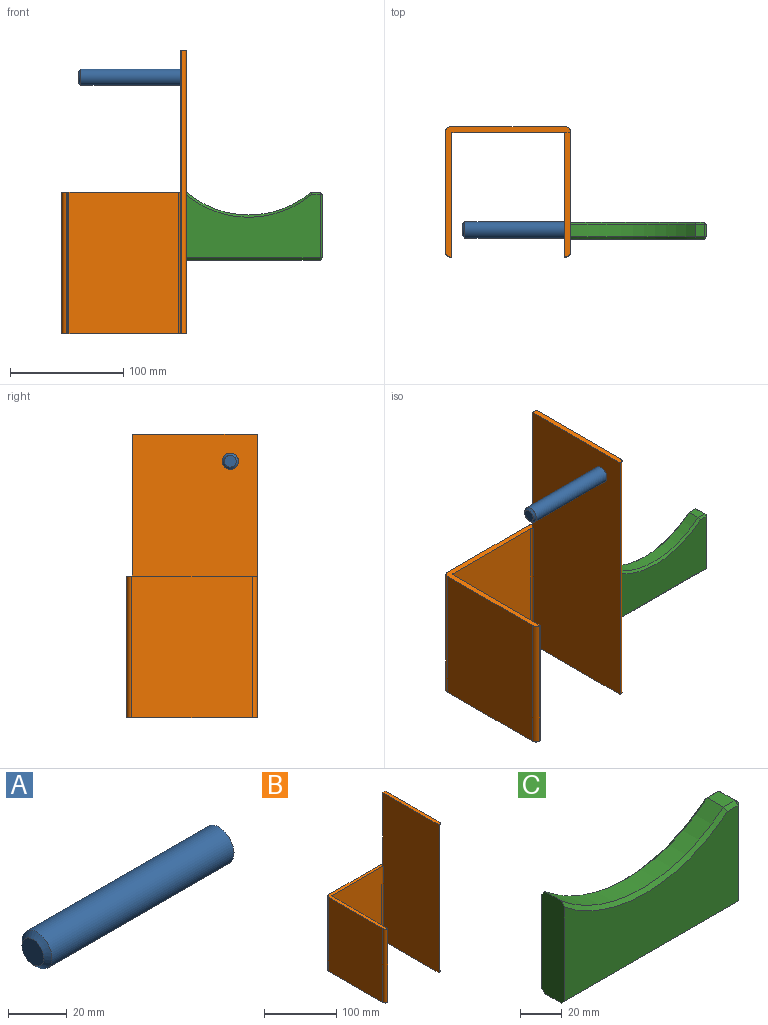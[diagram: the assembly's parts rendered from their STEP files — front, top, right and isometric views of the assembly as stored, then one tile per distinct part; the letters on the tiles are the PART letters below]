
ASSEMBLY  parts=3 mates=2
PART A: 4 faces, bbox 90x14.5x14.5 mm
  f0: cylinder r=7.25mm len=88mm, axis (-1,0,0), area 4008.7mm2, adj f1,f3
  f1: plane 14.5x14.5mm, normal (1,0,0), area 165.1mm2, adj f0
  f2: plane 10.5x10.5mm, normal (-1,0,0), area 86.6mm2, adj f3
  f3: cone r=7.25mm half-angle=45deg, axis (1,0,0), area 111.1mm2, adj f0,f2
PART B: 18 faces, bbox 110x115x250 mm
  f0: plane 250x106mm, normal (1,0,0), area 26437.5mm2, adj f1,f9,f10,f12,f13,f17
  f1: plane 110x5mm, normal (0,0,1), area 545.7mm2, adj f0,f3,f6,f12,f17
  f2: plane 125x0.5mm, normal (0,-1,0), area 62.5mm2, adj f4,f9,f10,f11
  f3: plane 250x0.5mm, normal (0,-1,0), area 125mm2, adj f1,f6,f9,f12
  f4: plane 125x108.5mm, normal (1,0,0), area 13562.5mm2, adj f2,f9,f10,f15
  f5: plane 125x97mm, normal (0,-1,0), area 12125mm2, adj f9,f10,f15,f16
  f6: plane 250x110mm, normal (-1,0,0), area 27312.5mm2, adj f1,f3,f9,f10,f16,f17
  f7: plane 125x106mm, normal (-1,0,0), area 13250mm2, adj f9,f10,f11,f14
  f8: plane 125x101mm, normal (0,1,0), area 12625mm2, adj f9,f10,f13,f14
  f9: plane 115x110mm, normal (0,0,-1), area 1633.6mm2, adj f0,f2,f3,f4,f5,f6,f7,f8
  f10: plane 115x110mm, normal (0,0,1), area 1087.9mm2, adj f0,f2,f4,f5,f6,f7,f8,f11
  f11: cylinder r=4.5mm len=125mm, axis (0,0,1), area 883.6mm2, adj f2,f7,f9,f10
  f12: cylinder r=4.5mm len=250mm, axis (0,0,-1), area 1767.1mm2, adj f0,f1,f3,f9
  f13: cylinder r=4.5mm len=125mm, axis (0,0,1), area 883.6mm2, adj f0,f8,f9,f10
  f14: cylinder r=4.5mm len=125mm, axis (0,0,-1), area 883.6mm2, adj f7,f8,f9,f10
  f15: cylinder r=1.5mm len=125mm, axis (0,0,-1), area 294.5mm2, adj f4,f5,f9,f10
  f16: cylinder r=1.5mm len=125mm, axis (0,0,1), area 294.5mm2, adj f5,f6,f9,f10
  f17: plane 125x5mm, normal (0,1,0), area 625mm2, adj f0,f1,f6,f10
PART C: 21 faces, bbox 121.3x15x60 mm
  f0: plane 11x8mm, normal (0,0,1), area 88mm2, adj f6,f10,f16,f19
  f1: plane 118x56mm, normal (0,-1,0), area 5069.1mm2, adj f5,f13,f17,f19,f20
  f2: plane 118x56mm, normal (0,1,0), area 5069.1mm2, adj f5,f7,f8,f10,f11
  f3: plane 118x11mm, normal (0,0,-1), area 1298mm2, adj f5,f7,f12,f13
  f4: plane 56x11mm, normal (1,0,0), area 616mm2, adj f11,f12,f16,f17
  f5: plane 60x15mm, normal (-1,0,0), area 890.8mm2, adj f1,f2,f3,f6,f7,f8,f13,f20
  f6: cylinder r=85mm len=110mm, axis (0,-1,0), area 1316mm2, adj f0,f5,f8,f20
  f7: plane 118x2mm, normal (0,0.71,-0.71), area 333.8mm2, adj f2,f3,f5,f9
  f8: cone r=87mm half-angle=45deg, axis (0,1,0), area 338.9mm2, adj f2,f5,f6,f10
  f9: plane 2x2mm, normal (0.58,0.58,-0.58), area 3.5mm2, adj f7,f11,f12
  f10: plane 8.01x2.01mm, normal (0,0.71,0.71), area 21.6mm2, adj f0,f2,f8,f14
  f11: plane 56x2mm, normal (0.71,0.71,0), area 158.4mm2, adj f2,f4,f9,f14
  f12: plane 11x2mm, normal (0.71,0,-0.71), area 31.1mm2, adj f3,f4,f9,f15
  f13: plane 118x2mm, normal (0,-0.71,-0.71), area 333.8mm2, adj f1,f3,f5,f15
  f14: plane 2x2mm, normal (0.58,0.58,0.58), area 3.5mm2, adj f10,f11,f16
  f15: plane 2x2mm, normal (0.58,-0.58,-0.58), area 3.5mm2, adj f12,f13,f17
  f16: plane 11x2mm, normal (0.71,0,0.71), area 31.1mm2, adj f0,f4,f14,f18
  f17: plane 56x2mm, normal (0.71,-0.71,0), area 158.4mm2, adj f1,f4,f15,f18
  f18: plane 2x2mm, normal (0.58,-0.58,0.58), area 3.5mm2, adj f16,f17,f19
  f19: plane 8.01x2.01mm, normal (0,-0.71,0.71), area 21.6mm2, adj f0,f1,f18,f20
  f20: cone r=85mm half-angle=45deg, axis (0,-1,0), area 338.9mm2, adj f1,f5,f6,f19
PLACE A t=(-289.83,279.13,54.13)mm
PLACE B at identity
PLACE C t=(-194.83,71.13,102.05)mm
MATE fastened C.f5 <-> B.f0  axis (-1,0,0) through (-194.83,-91.62,94.85)mm
MATE fastened A.f0 <-> B.f6  axis (1,0,0) through (-199.83,-91.25,226.25)mm
